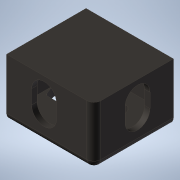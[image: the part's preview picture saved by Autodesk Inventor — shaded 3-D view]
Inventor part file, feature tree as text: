
AUTODESK INVENTOR PART (.ipt)
format: ipt  version: 2020 (Build 240168000, 168)  size: 159,744 bytes
history: mixed  units: mm
features: fillet x1, imported_body x1
ambient origin geometry x8: Origin, YZ Plane, XZ Plane, XY Plane, X Axis, Y Axis, Z Axis, Center Point
bodies: Solid1 (imported_parasolid)
feature tree (2):
  fillet  "Fillet1"  [1 undecoded]
  imported_body  NMx_Import_Brep_tag  [imported B-rep: ~42 faces, bbox_mm=[178.0, 118.0, 162.0]]
note: 1 required parameter value undecoded (feature->parameter linkage not recoverable at this tier; creation-order binding heuristic only, values carry confidence <= 0.55)
